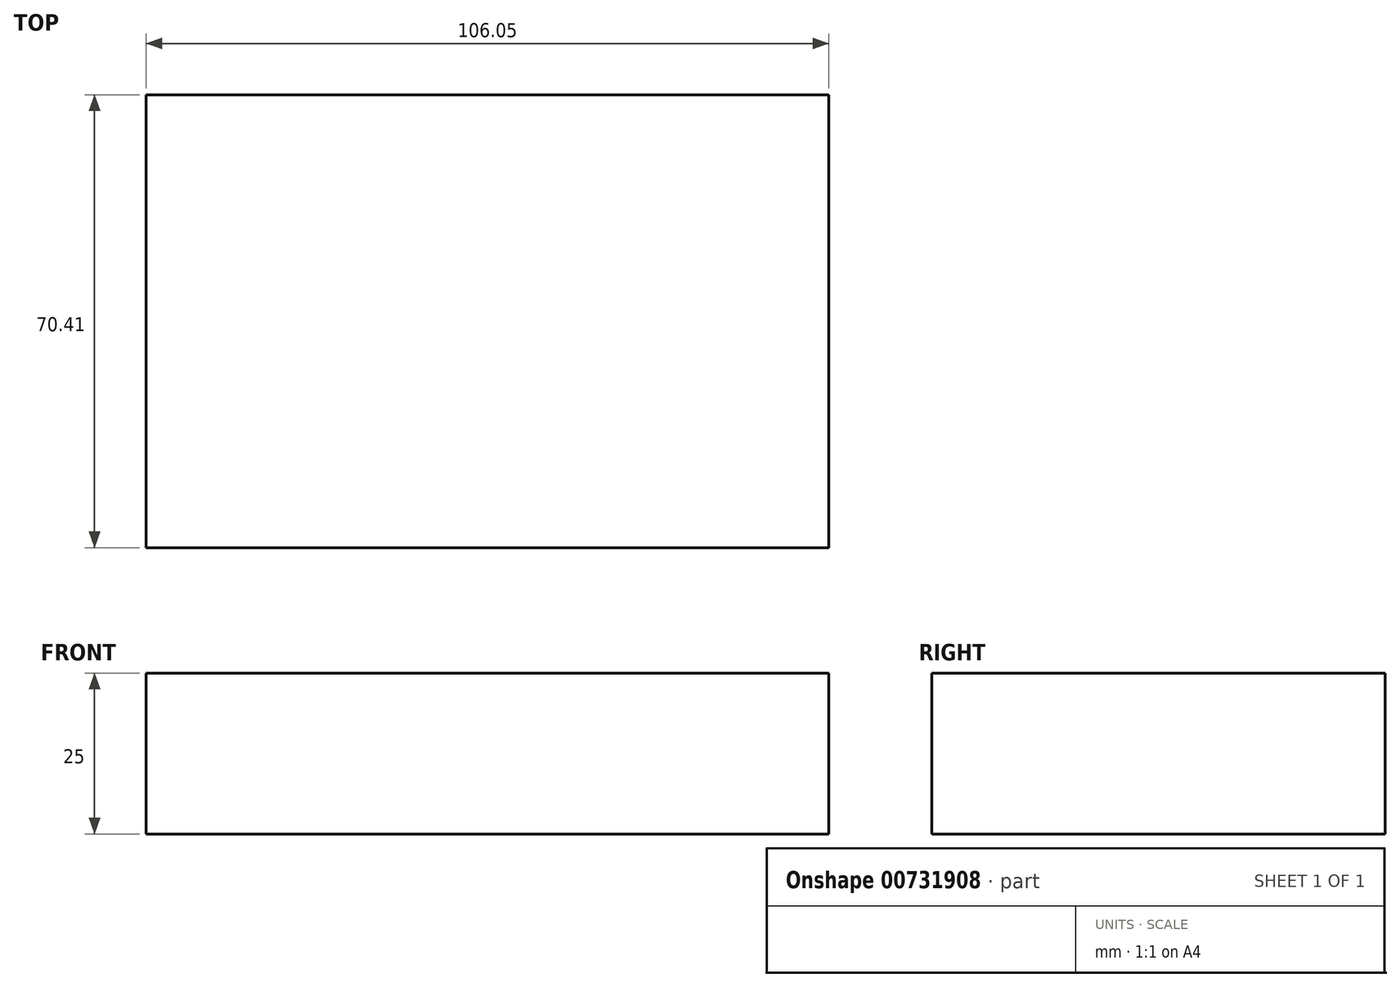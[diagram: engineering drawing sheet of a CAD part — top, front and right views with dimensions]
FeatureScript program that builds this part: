
annotation { "Feature Type Name" : "Feature", "Feature Type Description" : "" }
export const myFeature = defineFeature(function(context is Context, id is Id, definition is map)
    precondition{}
    {
        {
            var Q0;
            Q0=qCreatedBy(makeId("Top.planeOp"),FACE);
            var sketch = newSketch(context, id + "F0", { "sketchPlane" : qUnion([Q0])});
            skLineSegment(sketch, "E0.bottom", {"start": v(-30.2, 18) * mm, "end": v(75.85, 18) * mm});
            skLineSegment(sketch, "E0.top", {"start": v(-30.2, -52.42) * mm, "end": v(75.85, -52.42) * mm});
            skLineSegment(sketch, "E0.left", {"start": v(-30.2, 18) * mm, "end": v(-30.2, -52.42) * mm});
            skLineSegment(sketch, "E0.right", {"start": v(75.85, 18) * mm, "end": v(75.85, -52.42) * mm});
            skSolve(sketch);
        }
        {
            var Q0;
            Q0=makeQuery(id+"F0.imprint","IMPRINT",FACE,{"disambiguationData":[TD([[makeQuery(id+"F0.imprint","IMPRINT",EDGE,{"derivedFrom":sQuery(id+"F0.wireOp",EDGE,"E0.bottom")}),-1.0]])]});
            extrude(context, id + "F1", {"entities" : qUnion([Q0]), "depth" : 25 * mm, "offsetDistance" : 25 * mm});
        }
    });
